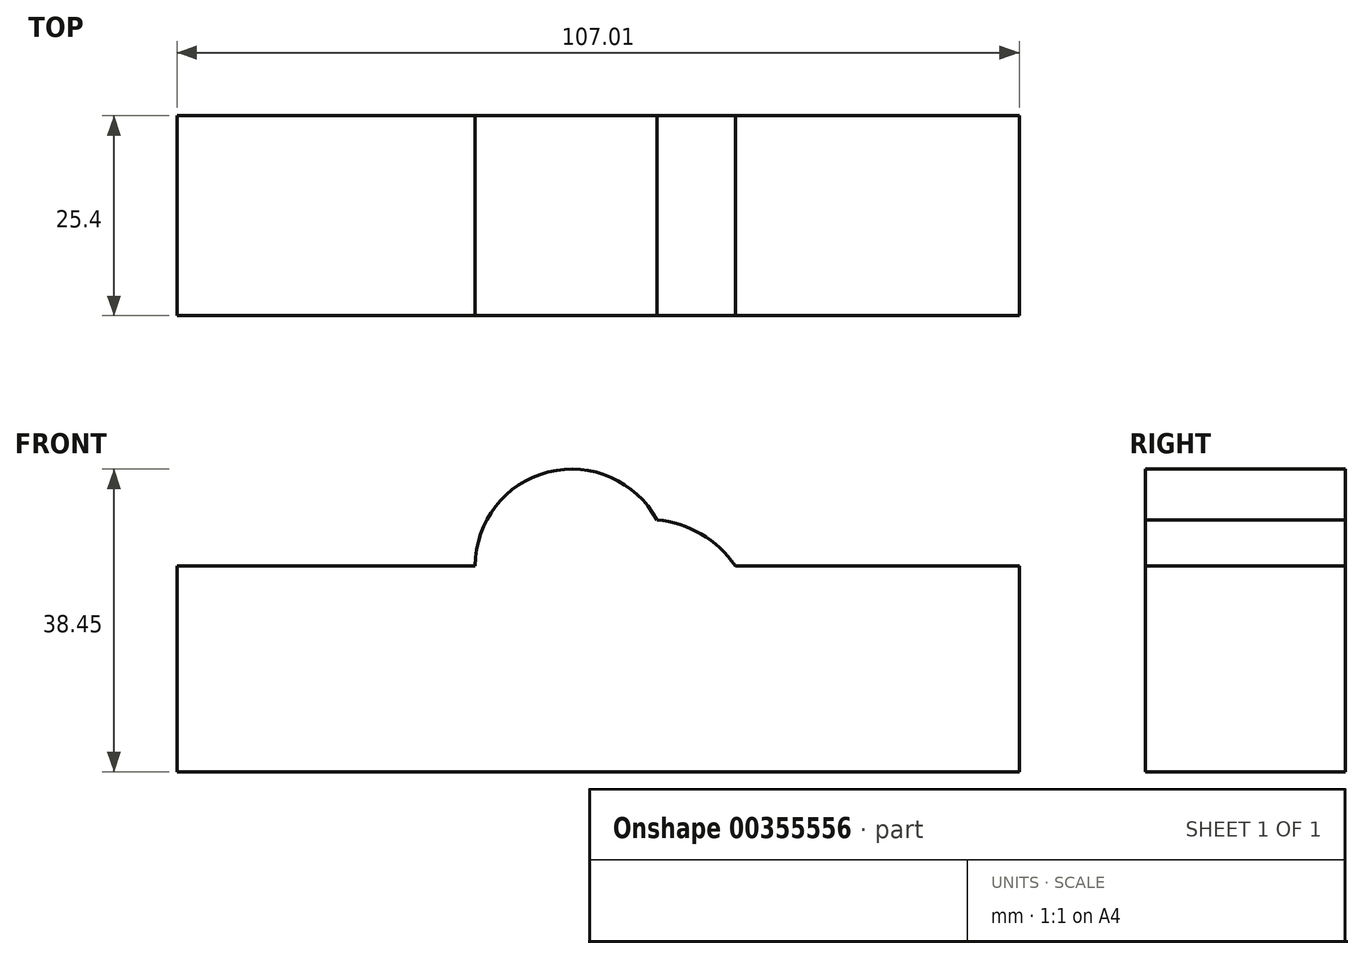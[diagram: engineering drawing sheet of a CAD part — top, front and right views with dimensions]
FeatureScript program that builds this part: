
annotation { "Feature Type Name" : "Feature", "Feature Type Description" : "" }
export const myFeature = defineFeature(function(context is Context, id is Id, definition is map)
    precondition{}
    {
        {
            var Q0;
            Q0=qCreatedBy(makeId("Front.planeOp"),FACE);
            var sketch = newSketch(context, id + "F0", { "sketchPlane" : qUnion([Q0])});
            skLineSegment(sketch, "E0", {"start": v(-50.17, 44) * mm, "end": v(-12.28, 44) * mm});
            skLineSegment(sketch, "E1", {"start": v(56.84, 44) * mm, "end": v(56.84, 17.83) * mm});
            skLineSegment(sketch, "E2", {"start": v(56.84, 17.83) * mm, "end": v(-50.17, 17.83) * mm});
            skLineSegment(sketch, "E3", {"start": v(-50.17, 44) * mm, "end": v(-50.17, 17.83) * mm});
            skArc(sketch, "E4", {"start": v(10.8, 49.83) * mm, "mid": v(-3, 55.9) * mm, "end": v(-12.28, 44) * mm});
            skArc(sketch, "E5", {"start": v(20.75, 44) * mm, "mid": v(16.42, 48.02) * mm, "end": v(10.8, 49.83) * mm});
            skLineSegment(sketch, "E6.trimOffspring", {"start": v(20.75, 44) * mm, "end": v(56.84, 44) * mm});
            skSolve(sketch);
        }
        {
            var Q0;
            Q0 = qSketchRegion(id + "F0", true);
            extrude(context, id + "F1", {"entities" : qUnion([Q0]), "depth" : 25.4 * mm});
        }
    });
